# Revit family: 2071491
name_source: partatom
category: Lighting Fixtures
units: mm (PartAtom-declared; Revit-internal decimal feet)

## family parameters
Cut with Voids When Loaded = No
Host = Face
Light Source = Yes
Maintain Annotation Orientation = No
OmniClass Number = 23.80.70.00
OmniClass Title = Lighting
Part Type = Normal
Room Calculation Point = No
Round Connector Dimension = Use Diameter
Shared = No

## types (1)
- MC2 TRIM 1.2M 4K DALI WHT OPAL
    Apparent Load = 18 VA
    Assembly Code = D5020200
    AssetType = Fixed
    ClassificationName = Uniclass2015
    ClassificationValue = EF_70_80
    Color Filter = 16777215
    Cost = 0 $
    Default Elevation = 1219 mm
    Description = MC2 TRIM 1.2M 4K DALI WHT OPAL LED luminaire, white RAL9016 finishing, direct distribution, trim detail for plasterboard ceilings, suitable for recessed installation either horizontally or vertically, various accessories available, compact and minimalist design based on the Golden Mean, ideal for offices, meeting rooms, corridors, education facilities, museums and libraries, extruded aluminium body, diffuser: opal, colour temperature: 4000K neutral white, total system power: 18W, total fixture output: 2400lm, luminaire efficacy: 133lm/W, LOR: 100%, colour rendering: Ra >80, LED Chromacity: 3 step MacAdam ellipse, lifespan: 66,000 hours L90B10, IR/UV free light source without heat radiation, operating voltage: 220-240V / 50-60Hz, drive current: 800mA, electronic driver, DALI dimmable, electrical protection: CLASS I, IP20, suitable for internal environment only.
    Dimming Lamp Color Temperature Shift = <None>
    DimmingControlOptions = DALI
    DocumentationLiterature = https://www.sylvania-lighting.com
    ElectricShockClassification = Class I
    EmergencyLight = No
    Emit Shape Visible in Rendering = No
    Emit from Rectangle Length = 1200 mm
    Emit from Rectangle Width = 54 mm  [stored 0.177165 ft]
    IfcExportAs = IfcLightFixtureType
    IfcExportType = IfcLightFixtureType
    ImpactProtectionIndex = IK03
    IngressProtection = IP20
    InputNominalFrequency = 50/60Hz
    InputVoltage = 220-240 V
    Keynote = 16500
    Lamp = LED
    LampColourRenderingIndex = 80
    LampColourTemperature = 4000 K
    LampMacAdamStep = 3
    LampNominalLuminous = 2400 lm
    LampsType = LED
    LightOutputRatio = 100
    LuminaireType = Ceiling recessed mounting
    LuminousEfficacy = 133 lm/W
    Manufacturer = Feilo Sylvania
    ManufacturerName = Feilo Sylvania
    Material = Aluminium
    Material_1_SYL = Metal_Sylvania_Mini Continuum II_White
    Material_2_SYL = Polycarbonate_Sylvania_Mini Continuum II_Opal_4000K
    Material_3_SYL = Metal_Sylvania_Mini Contiuum II_Silver
    Material_4_SYL = <By Category>
    Model = MC2 TRIM 1.2M 4K DALI WHT OPAL
    ModelNumber = 2071491
    ModelReference = MC2 TRIM 1.2M 4K DALI WHT OPAL
    Name = MC2 TRIM 1.2M 4K DALI WHT OPAL
    NominalDepth = 80 mm
    NominalHeight = 86 mm  [stored 0.282152 ft]
    NominalLength = 1200 mm
    Photometric Web File = 2071491.IES
    PowerConsumption = 18 W
    PowerFactor = 0.98
    Tilt Angle = -90.00°
    Type Image = <None>
    TypeName = Mini Continuum II - Direct - Trim
    URL = http://www.sylvania-group.com
    Voltage = 230 V
    WarrantyDescription = http://www.sylvania-group.com
    WarrantyDurationParts = 5
    WarrantyDurationUnit = Years
    Weight = 2.5 kg

note: [stored X ft] marks values corroborated as IEEE doubles in the binary element streams (Revit-internal decimal feet)

## geometry (parser evidence)
native form markers: Sweep x2
no freeform markers — native parametric forms only
